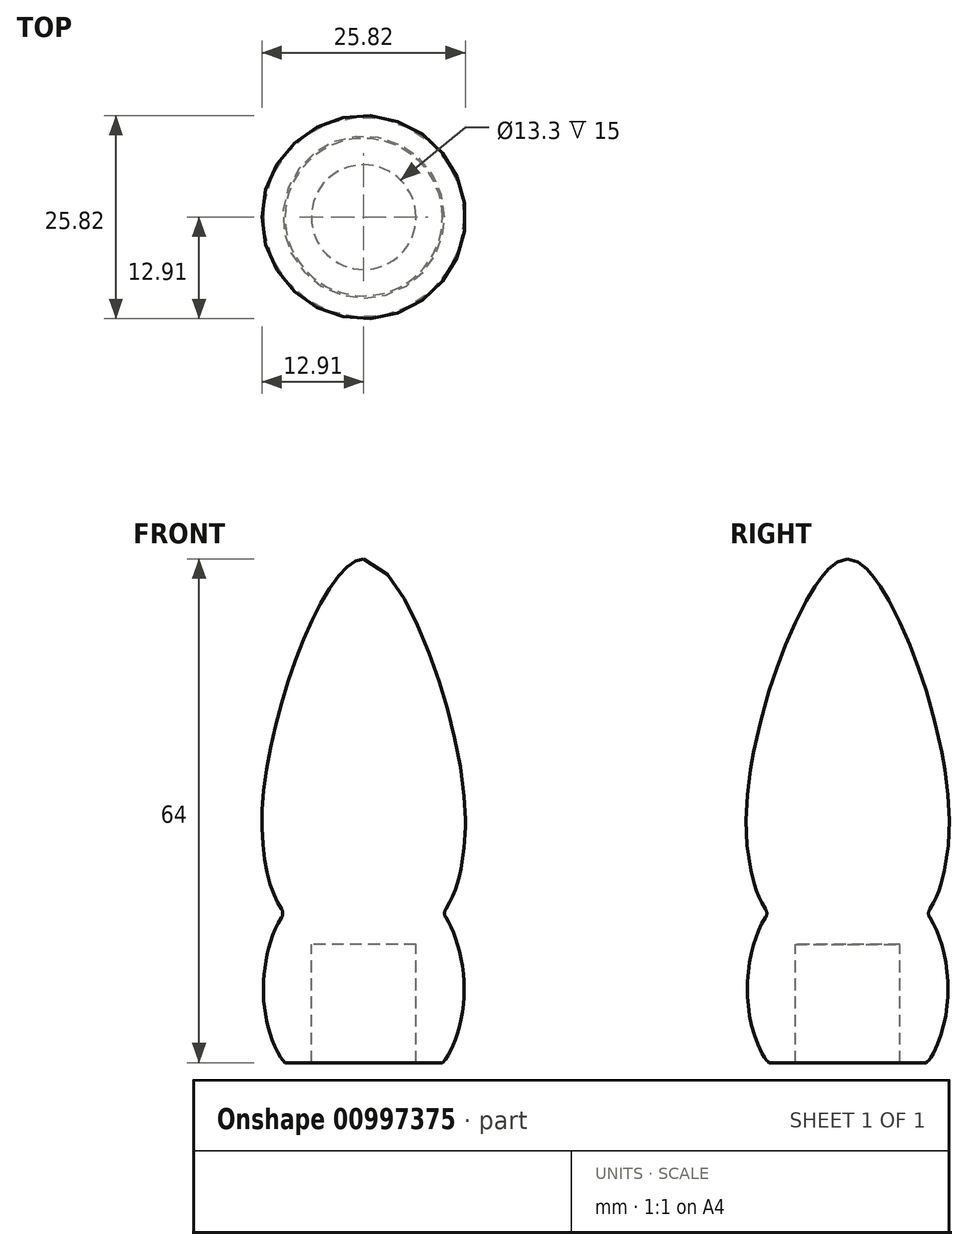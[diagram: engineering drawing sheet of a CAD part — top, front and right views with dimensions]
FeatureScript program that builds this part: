
annotation { "Feature Type Name" : "Feature", "Feature Type Description" : "" }
export const myFeature = defineFeature(function(context is Context, id is Id, definition is map)
    precondition{}
    {
        {
            var Q0;
            Q0=qCreatedBy(makeId("Front.planeOp"),FACE);
            var sketch = newSketch(context, id + "F0", { "sketchPlane" : qUnion([Q0])});
            skLineSegment(sketch, "E0", {"start": v(0, 0) * mm, "end": v(-12.75, 0) * mm, "construction": true});
            skLineSegment(sketch, "E1", {"start": v(-12.75, 0) * mm, "end": v(-12.75, 19) * mm, "construction": true});
            skLineSegment(sketch, "E2", {"start": v(-12.75, 19) * mm, "end": v(-12.75, 34) * mm, "construction": true});
            skLineSegment(sketch, "E3", {"start": v(-12.75, 34) * mm, "end": v(-12.75, 64) * mm, "construction": true});
            skLineSegment(sketch, "E4", {"start": v(-12.75, 64) * mm, "end": v(0, 64) * mm, "construction": true});
            skLineSegment(sketch, "E5", {"start": v(-12.75, 19) * mm, "end": v(0, 19) * mm, "construction": true});
            skPoint(sketch, "E6", {"position": v(-10, 19) * mm});
            skPoint(sketch, "E7", {"position": v(0, 0) * mm});
            skPoint(sketch, "E8", {"position": v(-10, 0) * mm});
            skLineSegment(sketch, "E9.left", {"start": v(0, 0) * mm, "end": v(0, 0) * mm});
            skLineSegment(sketch, "E10", {"start": v(0, 64) * mm, "end": v(0, 0) * mm, "construction": true});
            skFitSpline(sketch, "E11", {"points": [v(-10, 0) * mm, v(-12.75, 9.5) * mm, v(-10, 19) * mm], "startDerivative": vector(-9, 9) * mm, "endDerivative": vector(8.27, 9) * mm});
            skPoint(sketch, "E12", {"position": v(-6.65, 0) * mm});
            skLineSegment(sketch, "E13", {"start": v(-6.65, 0) * mm, "end": v(-6.65, 15) * mm});
            skLineSegment(sketch, "E14", {"start": v(-6.65, 15) * mm, "end": v(0, 15) * mm});
            skLineSegment(sketch, "E15", {"start": v(0, 15) * mm, "end": v(0, 64) * mm});
            skLineSegment(sketch, "E16", {"start": v(-6.65, 0) * mm, "end": v(-10, 0) * mm});
            skPoint(sketch, "E17", {"position": v(-12.75, 26.5) * mm});
            skFitSpline(sketch, "E18", {"points": [v(-10, 19) * mm, v(-12.75, 34) * mm, v(0, 64) * mm], "startDerivative": vector(-11.08, 11.08) * mm, "endDerivative": vector(23.88, 0) * mm});
            skSolve(sketch);
        }
        {
            var Q0;
            Q0=makeQuery(id+"F0.imprint","IMPRINT",FACE,{"disambiguationData":[TD([[makeQuery(id+"F0.imprint","IMPRINT",EDGE,{"derivedFrom":sQuery(id+"F0.wireOp",EDGE,"E11")}),-1.0]])]});
            var Q1;
            Q1=sQuery(id+"F0.wireOp",EDGE,"E10");
            revolve(context, id + "F1", {"surfaceOperationType" : NewSurfaceOperationType.NEW, "entities" : qUnion([Q0]), "axis" : qUnion([Q1]), "revolveType" : RevolveType.FULL});
        }
        {
            var Q0;
            Q0=makeQuery(id+"F1.opRevolve","SWEPT_EDGE",EDGE,{"disambiguationData":[OSD([sQuery(id+"F0.wireOp",EDGE,"E11"),sQuery(id+"F0.wireOp",EDGE,"E18")])]});
            fillet(context, id + "F2", {"entities" : qUnion([Q0]), "radius" : 1 * mm, "tangentPropagation" : true, "allowEdgeOverflow" : false});
        }
    });
